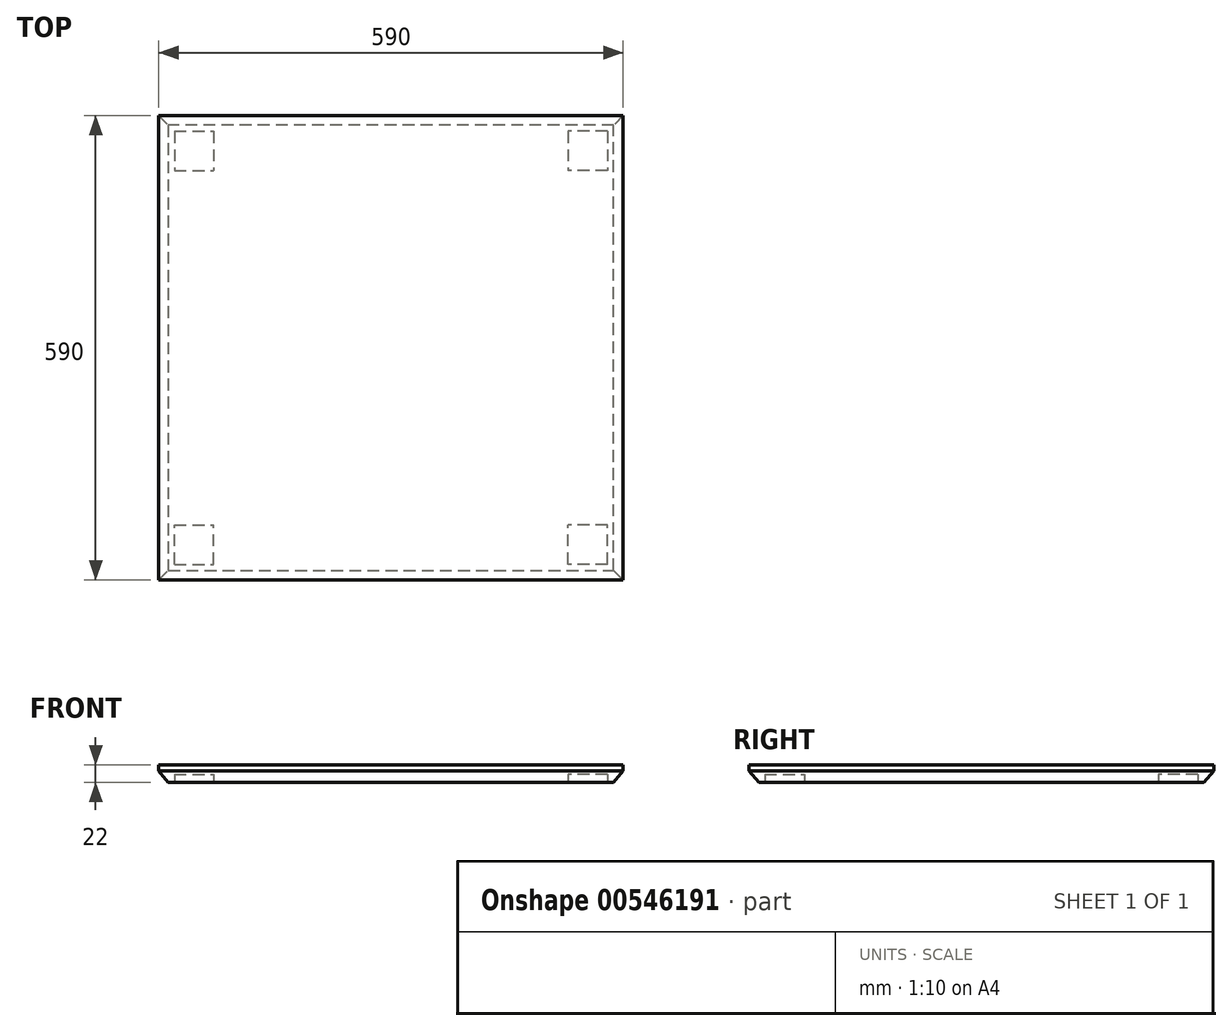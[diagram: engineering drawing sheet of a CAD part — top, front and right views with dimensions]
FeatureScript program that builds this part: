
annotation { "Feature Type Name" : "Feature", "Feature Type Description" : "" }
export const myFeature = defineFeature(function(context is Context, id is Id, definition is map)
    precondition{}
    {
        {
            var Q0;
            Q0=qCreatedBy(makeId("Top.planeOp"),FACE);
            var sketch = newSketch(context, id + "F0", { "sketchPlane" : qUnion([Q0])});
            skLineSegment(sketch, "E0.bottom", {"start": v(0, 0) * mm, "end": v(590, 0) * mm});
            skLineSegment(sketch, "E0.top", {"start": v(0, 590) * mm, "end": v(590, 590) * mm});
            skLineSegment(sketch, "E0.left", {"start": v(0, 0) * mm, "end": v(0, 590) * mm});
            skLineSegment(sketch, "E0.right", {"start": v(590, 0) * mm, "end": v(590, 590) * mm});
            skSolve(sketch);
        }
        {
            var Q0;
            Q0=makeQuery(id+"F0.imprint","IMPRINT",FACE,{"disambiguationData":[TD([[makeQuery(id+"F0.imprint","IMPRINT",EDGE,{"derivedFrom":sQuery(id+"F0.wireOp",EDGE,"E0.bottom")}),1.0]])]});
            extrude(context, id + "F1", {"entities" : qUnion([Q0]), "depth" : 22 * mm, "offsetDistance" : 25 * mm});
        }
        {
            var Q0;
            Q0=makeQuery(id+"F1.opExtrude","SWEPT_FACE",FACE,{"disambiguationData":[OSD([sQuery(id+"F0.wireOp",EDGE,"E0.right")])]});
            var sketch = newSketch(context, id + "F2", { "sketchPlane" : qUnion([Q0])});
            skSolve(sketch);
        }
        {
            var Q0;
            {var subQ0=sQuery(id+"F0.wireOp",EDGE,"E0.right");Q0=makeQuery(id+"F2.imprint","IMPRINT",FACE,{"disambiguationData":[TD([[makeQuery(id+"F2.imprint","IMPRINT",EDGE,{"derivedFrom":makeQuery(id+"F1.opExtrude","CAP_EDGE",EDGE,{"disambiguationData":[OSD([subQ0])],"isStart":true})}),1.0]])]});}
            var sketch = newSketch(context, id + "F3", { "sketchPlane" : qUnion([Q0])});
            skLineSegment(sketch, "E1.bottom", {"start": v(0, 0) * mm, "end": v(12.17, 0) * mm});
            skLineSegment(sketch, "E1.left", {"start": v(0, 0) * mm, "end": v(0, 14.5) * mm});
            skLineSegment(sketch, "E2", {"start": v(0, 14.5) * mm, "end": v(12.17, 0) * mm});
            skSolve(sketch);
        }
        {
            var Q0;
            Q0=makeQuery(id+"F1.opExtrude","SWEPT_FACE",FACE,{"disambiguationData":[OSD([sQuery(id+"F0.wireOp",EDGE,"E0.bottom")])]});
            var sketch = newSketch(context, id + "F4", { "sketchPlane" : qUnion([Q0])});
            skLineSegment(sketch, "E3.bottom", {"start": v(0, 0) * mm, "end": v(12.17, 0) * mm});
            skLineSegment(sketch, "E3.left", {"start": v(0, 0) * mm, "end": v(0, 14.5) * mm});
            skLineSegment(sketch, "E4", {"start": v(0, 14.5) * mm, "end": v(12.17, 0) * mm});
            skSolve(sketch);
        }
        {
            var Q0;
            Q0=makeQuery(id+"F1.opExtrude","SWEPT_FACE",FACE,{"disambiguationData":[OSD([sQuery(id+"F0.wireOp",EDGE,"E0.left")])]});
            var sketch = newSketch(context, id + "F5", { "sketchPlane" : qUnion([Q0])});
            skLineSegment(sketch, "E5.bottom", {"start": v(-590, 0) * mm, "end": v(-577.83, 0) * mm});
            skLineSegment(sketch, "E5.left", {"start": v(-590, 0) * mm, "end": v(-590, 14.5) * mm});
            skLineSegment(sketch, "E6", {"start": v(-590, 14.5) * mm, "end": v(-577.83, 0) * mm});
            skSolve(sketch);
        }
        {
            var Q0;
            Q0=makeQuery(id+"F1.opExtrude","SWEPT_FACE",FACE,{"disambiguationData":[OSD([sQuery(id+"F0.wireOp",EDGE,"E0.top")])]});
            var sketch = newSketch(context, id + "F6", { "sketchPlane" : qUnion([Q0])});
            skLineSegment(sketch, "E7.bottom", {"start": v(-590, 0) * mm, "end": v(-577.83, 0) * mm});
            skLineSegment(sketch, "E7.left", {"start": v(-590, 0) * mm, "end": v(-590, 14.5) * mm});
            skLineSegment(sketch, "E8", {"start": v(-590, 14.5) * mm, "end": v(-577.83, 0) * mm});
            skSolve(sketch);
        }
        {
            var Q0;
            Q0 = qSketchRegion(id + "F3", true);
            extrude(context, id + "F7", {"entities" : qUnion([Q0]), "operationType" : NewBodyOperationType.REMOVE, "endBound" : BoundingType.THROUGH_ALL, "oppositeDirection" : true, "depth" : 25 * mm, "offsetDistance" : 25 * mm});
        }
        {
            var Q0;
            Q0 = qSketchRegion(id + "F4", true);
            extrude(context, id + "F8", {"entities" : qUnion([Q0]), "operationType" : NewBodyOperationType.REMOVE, "endBound" : BoundingType.THROUGH_ALL, "oppositeDirection" : true, "depth" : 25 * mm, "offsetDistance" : 25 * mm});
        }
        {
            var Q0;
            Q0 = qSketchRegion(id + "F5", true);
            extrude(context, id + "F9", {"entities" : qUnion([Q0]), "operationType" : NewBodyOperationType.REMOVE, "endBound" : BoundingType.THROUGH_ALL, "oppositeDirection" : true, "depth" : 25 * mm, "offsetDistance" : 25 * mm});
        }
        {
            var Q0;
            Q0 = qSketchRegion(id + "F6", true);
            extrude(context, id + "F10", {"entities" : qUnion([Q0]), "operationType" : NewBodyOperationType.REMOVE, "endBound" : BoundingType.THROUGH_ALL, "oppositeDirection" : true, "depth" : 25 * mm, "offsetDistance" : 25 * mm});
        }
        {
            var Q0;
            Q0=makeQuery(id+"F1.opExtrude","CAP_FACE",FACE,{"disambiguationData":[OSD([sQuery(id+"F0.wireOp",EDGE,"E0.bottom"),sQuery(id+"F0.wireOp",EDGE,"E0.top"),sQuery(id+"F0.wireOp",EDGE,"E0.left"),sQuery(id+"F0.wireOp",EDGE,"E0.right")])],"isStart":true});
            var sketch = newSketch(context, id + "F11", { "sketchPlane" : qUnion([Q0])});
            skLineSegment(sketch, "E9.bottom", {"start": v(12.17, -12.17) * mm, "end": v(19.97, -12.17) * mm});
            skLineSegment(sketch, "E9.top", {"start": v(12.17, -19.97) * mm, "end": v(19.97, -19.97) * mm});
            skLineSegment(sketch, "E9.left", {"start": v(12.17, -12.17) * mm, "end": v(12.17, -19.97) * mm});
            skLineSegment(sketch, "E9.right", {"start": v(19.97, -12.17) * mm, "end": v(19.97, -19.97) * mm});
            skLineSegment(sketch, "E10.bottom", {"start": v(19.97, -19.97) * mm, "end": v(69.97, -19.97) * mm});
            skLineSegment(sketch, "E10.top", {"start": v(19.97, -69.97) * mm, "end": v(69.97, -69.97) * mm});
            skLineSegment(sketch, "E10.left", {"start": v(19.97, -19.97) * mm, "end": v(19.97, -69.97) * mm});
            skLineSegment(sketch, "E10.right", {"start": v(69.97, -19.97) * mm, "end": v(69.97, -69.97) * mm});
            skLineSegment(sketch, "E11.bottom", {"start": v(577.83, -12.17) * mm, "end": v(570.03, -12.17) * mm});
            skLineSegment(sketch, "E11.top", {"start": v(577.83, -19.97) * mm, "end": v(570.03, -19.97) * mm});
            skLineSegment(sketch, "E11.left", {"start": v(577.83, -12.17) * mm, "end": v(577.83, -19.97) * mm});
            skLineSegment(sketch, "E11.right", {"start": v(570.03, -12.17) * mm, "end": v(570.03, -19.97) * mm});
            skLineSegment(sketch, "E12.bottom", {"start": v(570.03, -19.97) * mm, "end": v(520.03, -19.97) * mm});
            skLineSegment(sketch, "E12.top", {"start": v(570.03, -69.97) * mm, "end": v(520.03, -69.97) * mm});
            skLineSegment(sketch, "E12.left", {"start": v(570.03, -19.97) * mm, "end": v(570.03, -69.97) * mm});
            skLineSegment(sketch, "E12.right", {"start": v(520.03, -19.97) * mm, "end": v(520.03, -69.97) * mm});
            skLineSegment(sketch, "E13.bottom", {"start": v(12.17, -577.83) * mm, "end": v(19.97, -577.83) * mm});
            skLineSegment(sketch, "E13.top", {"start": v(12.17, -570.03) * mm, "end": v(19.97, -570.03) * mm});
            skLineSegment(sketch, "E13.left", {"start": v(12.17, -577.83) * mm, "end": v(12.17, -570.03) * mm});
            skLineSegment(sketch, "E13.right", {"start": v(19.97, -577.83) * mm, "end": v(19.97, -570.03) * mm});
            skLineSegment(sketch, "E14.bottom", {"start": v(19.97, -570.03) * mm, "end": v(69.97, -570.03) * mm});
            skLineSegment(sketch, "E14.top", {"start": v(19.97, -520.03) * mm, "end": v(69.97, -520.03) * mm});
            skLineSegment(sketch, "E14.left", {"start": v(19.97, -570.03) * mm, "end": v(19.97, -520.03) * mm});
            skLineSegment(sketch, "E14.right", {"start": v(69.97, -570.03) * mm, "end": v(69.97, -520.03) * mm});
            skLineSegment(sketch, "E15.bottom", {"start": v(577.83, -577.83) * mm, "end": v(570.03, -577.83) * mm});
            skLineSegment(sketch, "E15.top", {"start": v(577.83, -570.03) * mm, "end": v(570.03, -570.03) * mm});
            skLineSegment(sketch, "E15.left", {"start": v(577.83, -577.83) * mm, "end": v(577.83, -570.03) * mm});
            skLineSegment(sketch, "E15.right", {"start": v(570.03, -577.83) * mm, "end": v(570.03, -570.03) * mm});
            skLineSegment(sketch, "E16.bottom", {"start": v(570.03, -570.03) * mm, "end": v(520.03, -570.03) * mm});
            skLineSegment(sketch, "E16.top", {"start": v(570.03, -520.03) * mm, "end": v(520.03, -520.03) * mm});
            skLineSegment(sketch, "E16.left", {"start": v(570.03, -570.03) * mm, "end": v(570.03, -520.03) * mm});
            skLineSegment(sketch, "E16.right", {"start": v(520.03, -570.03) * mm, "end": v(520.03, -520.03) * mm});
            skSolve(sketch);
        }
        {
            var Q0;
            Q0=makeQuery(id+"F11.imprint","IMPRINT",FACE,{"disambiguationData":[TD([[makeQuery(id+"F11.imprint","IMPRINT",EDGE,{"derivedFrom":sQuery(id+"F11.wireOp",EDGE,"E10.bottom")}),-1.0]])]});
            var Q1;
            Q1=makeQuery(id+"F11.imprint","IMPRINT",FACE,{"disambiguationData":[TD([[makeQuery(id+"F11.imprint","IMPRINT",EDGE,{"derivedFrom":sQuery(id+"F11.wireOp",EDGE,"E12.bottom")}),1.0]])]});
            var Q2;
            Q2=makeQuery(id+"F11.imprint","IMPRINT",FACE,{"disambiguationData":[TD([[makeQuery(id+"F11.imprint","IMPRINT",EDGE,{"derivedFrom":sQuery(id+"F11.wireOp",EDGE,"E14.bottom")}),1.0]])]});
            var Q3;
            Q3=makeQuery(id+"F11.imprint","IMPRINT",FACE,{"disambiguationData":[TD([[makeQuery(id+"F11.imprint","IMPRINT",EDGE,{"derivedFrom":sQuery(id+"F11.wireOp",EDGE,"E16.bottom")}),-1.0]])]});
            extrude(context, id + "F12", {"entities" : qUnion([Q0, Q1, Q2, Q3]), "operationType" : NewBodyOperationType.REMOVE, "oppositeDirection" : true, "depth" : 10 * mm, "offsetDistance" : 25 * mm});
        }
    });
